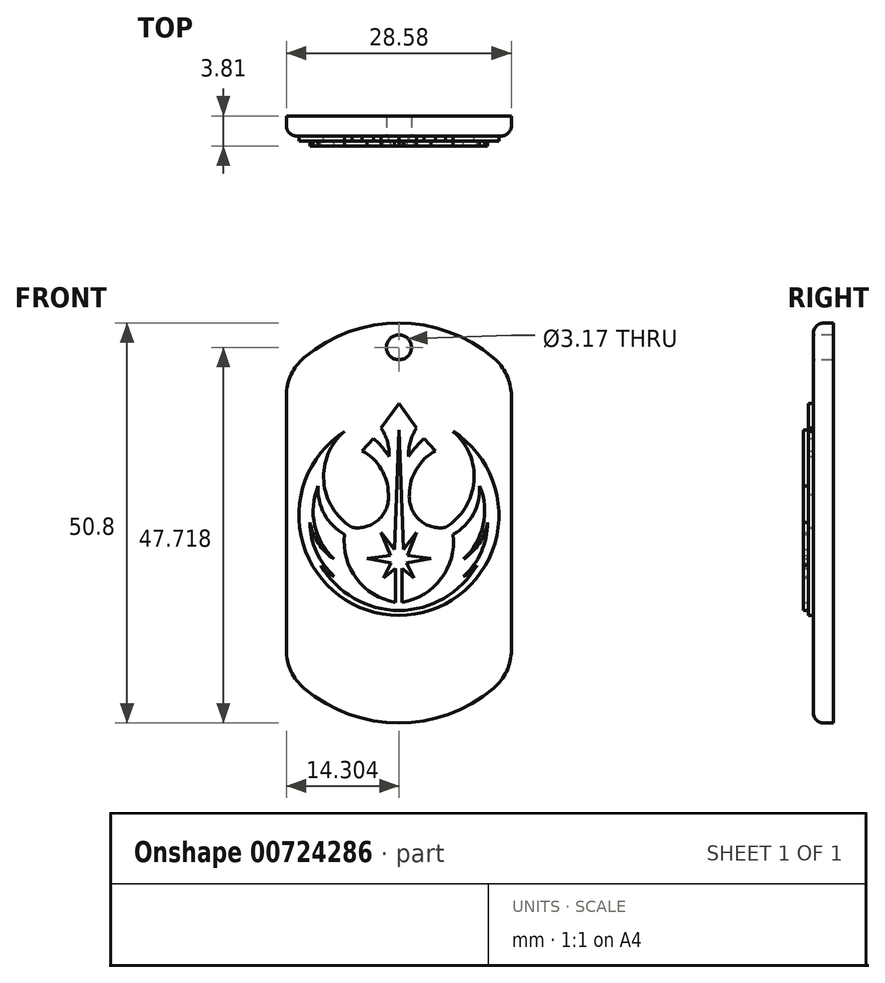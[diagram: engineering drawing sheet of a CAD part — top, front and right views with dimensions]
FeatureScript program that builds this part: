
annotation { "Feature Type Name" : "Feature", "Feature Type Description" : "" }
export const myFeature = defineFeature(function(context is Context, id is Id, definition is map)
    precondition{}
    {
        {
            var Q0;
            Q0=qCreatedBy(makeId("Front.planeOp"),FACE);
            var sketch = newSketch(context, id + "F0", { "sketchPlane" : qUnion([Q0])});
            skLineSegment(sketch, "E0.left", {"start": v(0, 2.6) * mm, "end": v(0, 34.89) * mm});
            skLineSegment(sketch, "E0.right", {"start": v(-28.58, 2.6) * mm, "end": v(-28.58, 34.91) * mm});
            skArc(sketch, "E1", {"start": v(-2.25, 39.74) * mm, "mid": v(-14.27, 44.15) * mm, "end": v(-26.3, 39.77) * mm});
            skArc(sketch, "E2", {"start": v(-26.32, -2.26) * mm, "mid": v(-14.29, -6.65) * mm, "end": v(-2.26, -2.26) * mm});
            skPoint(sketch, "E3.visualSharp", {"position": v(0, 37.48) * mm});
            skArc(sketch, "E3.filletArc", {"start": v(0, 34.89) * mm, "mid": v(-0.6, 37.56) * mm, "end": v(-2.25, 39.74) * mm});
            skPoint(sketch, "E4.visualSharp", {"position": v(-28.58, 37.51) * mm});
            skArc(sketch, "E4.filletArc", {"start": v(-26.3, 39.77) * mm, "mid": v(-27.98, 37.6) * mm, "end": v(-28.57, 34.91) * mm});
            skPoint(sketch, "E5.visualSharp", {"position": v(-28.58, 0) * mm});
            skArc(sketch, "E5.filletArc", {"start": v(-28.57, 2.6) * mm, "mid": v(-27.98, -0.08) * mm, "end": v(-26.32, -2.26) * mm});
            skPoint(sketch, "E6.visualSharp", {"position": v(0, 0) * mm});
            skArc(sketch, "E6.filletArc", {"start": v(-2.26, -2.26) * mm, "mid": v(-0.6, -0.08) * mm, "end": v(0, 2.6) * mm});
            skSolve(sketch);
        }
        {
            var Q0;
            Q0=makeQuery(id+"F0.imprint","IMPRINT",FACE,{"disambiguationData":[TD([[makeQuery(id+"F0.imprint","IMPRINT",EDGE,{"derivedFrom":sQuery(id+"F0.wireOp",EDGE,"E0.left")}),1.0]])]});
            extrude(context, id + "F1", {"entities" : qUnion([Q0]), "depth" : 2.54 * mm, "offsetDistance" : 25.4 * mm});
        }
        {
            var Q0;
            Q0=makeQuery(id+"F1.opExtrude","CAP_EDGE",EDGE,{"disambiguationData":[OSD([sQuery(id+"F0.wireOp",EDGE,"E1")])],"isStart":false});
            fillet(context, id + "F2", {"entities" : qUnion([Q0]), "radius" : 1.27 * mm, "tangentPropagation" : true, "allowEdgeOverflow" : false});
        }
        {
            var Q0;
            Q0=makeQuery(id+"F1.opExtrude","CAP_FACE",FACE,{"disambiguationData":[OSD([sQuery(id+"F0.wireOp",EDGE,"E0.left"),sQuery(id+"F0.wireOp",EDGE,"E0.right"),sQuery(id+"F0.wireOp",EDGE,"E1"),sQuery(id+"F0.wireOp",EDGE,"E2"),sQuery(id+"F0.wireOp",EDGE,"E3.filletArc"),sQuery(id+"F0.wireOp",EDGE,"E4.filletArc"),sQuery(id+"F0.wireOp",EDGE,"E5.filletArc"),sQuery(id+"F0.wireOp",EDGE,"E6.filletArc")])],"isStart":false});
            var sketch = newSketch(context, id + "F3", { "sketchPlane" : qUnion([Q0])});
            skCircle(sketch, "E7", {"center": v(-14.28, 41.07) * mm, "radius": 1.59 * mm});
            skPoint(sketch, "E8", {"position": v(-14.28, 42.88) * mm});
            skSolve(sketch);
        }
        {
            var Q0;
            Q0=makeQuery(id+"F3.imprint","IMPRINT",FACE,{"disambiguationData":[TD([[makeQuery(id+"F3.imprint","IMPRINT",EDGE,{"derivedFrom":sQuery(id+"F3.wireOp",EDGE,"E7")}),1.0]])]});
            extrude(context, id + "F4", {"entities" : qUnion([Q0]), "operationType" : NewBodyOperationType.REMOVE, "oppositeDirection" : true, "depth" : 25.4 * mm, "offsetDistance" : 25.4 * mm});
        }
        {
            var Q0;
            Q0=makeQuery(id+"F1.opExtrude","CAP_FACE",FACE,{"disambiguationData":[OSD([sQuery(id+"F0.wireOp",EDGE,"E0.left"),sQuery(id+"F0.wireOp",EDGE,"E0.right"),sQuery(id+"F0.wireOp",EDGE,"E1"),sQuery(id+"F0.wireOp",EDGE,"E2"),sQuery(id+"F0.wireOp",EDGE,"E3.filletArc"),sQuery(id+"F0.wireOp",EDGE,"E4.filletArc"),sQuery(id+"F0.wireOp",EDGE,"E5.filletArc"),sQuery(id+"F0.wireOp",EDGE,"E6.filletArc")])],"isStart":false});
            var sketch = newSketch(context, id + "F5", { "sketchPlane" : qUnion([Q0])});
            skArc(sketch, "E9", {"start": v(-21.17, 30.4) * mm, "mid": v(-14.3, 7.03) * mm, "end": v(-7.4, 30.4) * mm});
            skArc(sketch, "E10", {"start": v(-24.55, 23.44) * mm, "mid": v(-23.75, 19.87) * mm, "end": v(-21.18, 17.28) * mm});
            skArc(sketch, "E11", {"start": v(-24.55, 23.44) * mm, "mid": v(-24.99, 18.48) * mm, "end": v(-22.5, 14.16) * mm});
            skArc(sketch, "E12", {"start": v(-25.57, 18.8) * mm, "mid": v(-24.5, 16.16) * mm, "end": v(-22.5, 14.16) * mm});
            skArc(sketch, "E13", {"start": v(-25.57, 18.8) * mm, "mid": v(-24.76, 15.06) * mm, "end": v(-22.5, 11.98) * mm});
            skArc(sketch, "E14", {"start": v(-24.2, 13.37) * mm, "mid": v(-23.45, 12.56) * mm, "end": v(-22.5, 11.98) * mm});
            skArc(sketch, "E15", {"start": v(-24.2, 13.37) * mm, "mid": v(-20, 9.2) * mm, "end": v(-14.3, 7.63) * mm});
            skArc(sketch, "E16", {"start": v(-21.18, 17.28) * mm, "mid": v(-19.67, 11.68) * mm, "end": v(-14.7, 8.68) * mm});
            skArc(sketch, "E17", {"start": v(-15.54, 27.2) * mm, "mid": v(-15.75, 29.1) * mm, "end": v(-16.56, 30.83) * mm});
            skArc(sketch, "E18", {"start": v(-15.54, 27.2) * mm, "mid": v(-16.45, 28.41) * mm, "end": v(-17.5, 29.5) * mm});
            skArc(sketch, "E19", {"start": v(-21.17, 30.4) * mm, "mid": v(-23.83, 24.06) * mm, "end": v(-20.23, 18.2) * mm});
            skArc(sketch, "E20", {"start": v(-20.23, 18.2) * mm, "mid": v(-16.9, 19.15) * mm, "end": v(-15.62, 22.38) * mm});
            skArc(sketch, "E21", {"start": v(-15.62, 22.38) * mm, "mid": v(-16.53, 25.6) * mm, "end": v(-18.95, 27.93) * mm});
            skLineSegment(sketch, "E22", {"start": v(-18.95, 27.93) * mm, "end": v(-17.5, 29.5) * mm});
            skLineSegment(sketch, "E23", {"start": v(-16.56, 30.83) * mm, "end": v(-14.3, 33.9) * mm});
            skLineSegment(sketch, "E24", {"start": v(-14.7, 8.68) * mm, "end": v(-14.7, 12.98) * mm});
            skLineSegment(sketch, "E25", {"start": v(-14.7, 12.98) * mm, "end": v(-16.22, 11.79) * mm});
            skLineSegment(sketch, "E26", {"start": v(-16.22, 11.79) * mm, "end": v(-15.26, 13.7) * mm});
            skLineSegment(sketch, "E27", {"start": v(-15.26, 13.7) * mm, "end": v(-18.36, 14.26) * mm});
            skLineSegment(sketch, "E28", {"start": v(-18.36, 14.26) * mm, "end": v(-15.36, 14.62) * mm});
            skLineSegment(sketch, "E29", {"start": v(-15.36, 14.62) * mm, "end": v(-16.54, 17.54) * mm});
            skLineSegment(sketch, "E30", {"start": v(-16.54, 17.54) * mm, "end": v(-14.87, 15.39) * mm});
            skLineSegment(sketch, "E31", {"start": v(-14.87, 15.39) * mm, "end": v(-14.3, 30.55) * mm});
            skLineSegment(sketch, "E32.MirrorCS", {"start": v(-12.02, 30.83) * mm, "end": v(-14.3, 33.9) * mm});
            skArc(sketch, "E33.MirrorCS", {"start": v(-13.04, 27.2) * mm, "mid": v(-12.13, 28.41) * mm, "end": v(-11.08, 29.5) * mm});
            skLineSegment(sketch, "E34.MirrorCS", {"start": v(-9.63, 27.93) * mm, "end": v(-11.08, 29.5) * mm});
            skArc(sketch, "E35.MirrorCS", {"start": v(-12.96, 22.38) * mm, "mid": v(-12.05, 25.6) * mm, "end": v(-9.63, 27.93) * mm});
            skArc(sketch, "E36.MirrorCS", {"start": v(-8.35, 18.2) * mm, "mid": v(-11.68, 19.15) * mm, "end": v(-12.96, 22.38) * mm});
            skArc(sketch, "E37.MirrorCS", {"start": v(-7.4, 30.4) * mm, "mid": v(-4.75, 24.06) * mm, "end": v(-8.35, 18.2) * mm});
            skArc(sketch, "E38.MirrorCS", {"start": v(-4.03, 23.44) * mm, "mid": v(-4.83, 19.87) * mm, "end": v(-7.4, 17.28) * mm});
            skArc(sketch, "E39.MirrorCS", {"start": v(-4.03, 23.44) * mm, "mid": v(-3.6, 18.48) * mm, "end": v(-6.08, 14.16) * mm});
            skArc(sketch, "E40.MirrorCS", {"start": v(-3, 18.8) * mm, "mid": v(-4.08, 16.16) * mm, "end": v(-6.08, 14.16) * mm});
            skArc(sketch, "E41.MirrorCS", {"start": v(-3, 18.8) * mm, "mid": v(-3.82, 15.06) * mm, "end": v(-6.08, 11.98) * mm});
            skArc(sketch, "E42.MirrorCS", {"start": v(-4.38, 13.37) * mm, "mid": v(-5.13, 12.56) * mm, "end": v(-6.08, 11.98) * mm});
            skArc(sketch, "E43.MirrorCS", {"start": v(-4.38, 13.37) * mm, "mid": v(-8.58, 9.2) * mm, "end": v(-14.3, 7.63) * mm});
            skLineSegment(sketch, "E44.MirrorCS", {"start": v(-13.87, 8.68) * mm, "end": v(-13.87, 12.98) * mm});
            skLineSegment(sketch, "E45.MirrorCS", {"start": v(-13.87, 12.98) * mm, "end": v(-12.36, 11.79) * mm});
            skLineSegment(sketch, "E46.MirrorCS", {"start": v(-12.36, 11.79) * mm, "end": v(-13.32, 13.7) * mm});
            skLineSegment(sketch, "E47.MirrorCS", {"start": v(-13.32, 13.7) * mm, "end": v(-10.23, 14.26) * mm});
            skLineSegment(sketch, "E48.MirrorCS", {"start": v(-10.23, 14.26) * mm, "end": v(-13.22, 14.62) * mm});
            skLineSegment(sketch, "E49.MirrorCS", {"start": v(-13.22, 14.62) * mm, "end": v(-12.04, 17.54) * mm});
            skLineSegment(sketch, "E50.MirrorCS", {"start": v(-12.04, 17.54) * mm, "end": v(-13.7, 15.39) * mm});
            skLineSegment(sketch, "E51.MirrorCS", {"start": v(-13.7, 15.39) * mm, "end": v(-14.3, 30.55) * mm});
            skArc(sketch, "E52.MirrorCS", {"start": v(-13.04, 27.2) * mm, "mid": v(-12.83, 29.1) * mm, "end": v(-12.02, 30.83) * mm});
            skArc(sketch, "E53.MirrorCS", {"start": v(-7.4, 17.28) * mm, "mid": v(-8.91, 11.68) * mm, "end": v(-13.87, 8.68) * mm});
            skSolve(sketch);
        }
        {
            var Q0;
            Q0=makeQuery(id+"F5.imprint","IMPRINT",FACE,{"disambiguationData":[TD([[makeQuery(id+"F5.imprint","IMPRINT",EDGE,{"derivedFrom":sQuery(id+"F5.wireOp",EDGE,"E10")}),-1.0]])]});
            extrude(context, id + "F6", {"entities" : qUnion([Q0]), "operationType" : NewBodyOperationType.ADD, "depth" : 1.27 * mm, "offsetDistance" : 25.4 * mm});
        }
        {
            var Q0;
            Q0=makeQuery(id+"F5.imprint","IMPRINT",FACE,{"disambiguationData":[TD([[makeQuery(id+"F5.imprint","IMPRINT",EDGE,{"derivedFrom":sQuery(id+"F5.wireOp",EDGE,"E9")}),1.0]])]});
            extrude(context, id + "F7", {"entities" : qUnion([Q0]), "operationType" : NewBodyOperationType.ADD, "depth" : 0.64 * mm, "offsetDistance" : 25.4 * mm});
        }
    });
